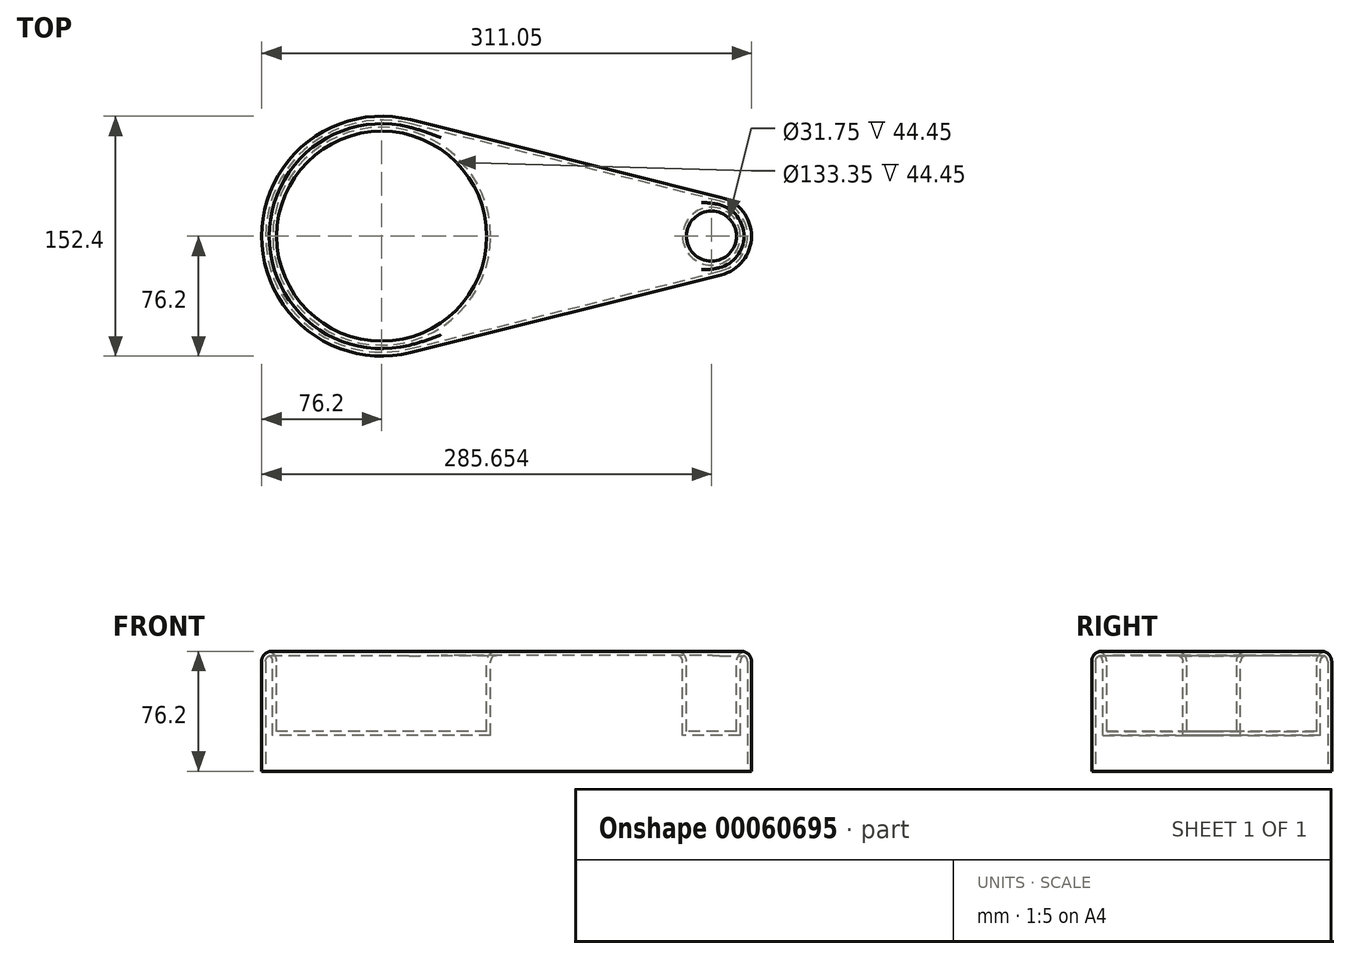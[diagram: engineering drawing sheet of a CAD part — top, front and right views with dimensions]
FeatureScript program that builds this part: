
annotation { "Feature Type Name" : "Feature", "Feature Type Description" : "" }
export const myFeature = defineFeature(function(context is Context, id is Id, definition is map)
    precondition{}
    {
        {
            var Q0;
            Q0=qCreatedBy(makeId("Top.planeOp"),FACE);
            var sketch = newSketch(context, id + "F0", { "sketchPlane" : qUnion([Q0])});
            skCircle(sketch, "E0", {"center": v(0, 0) * mm, "radius": 76.2 * mm});
            skCircle(sketch, "E1", {"center": v(209.45, 0) * mm, "radius": 25.4 * mm});
            skLineSegment(sketch, "E2", {"start": v(215.61, 24.64) * mm, "end": v(18.48, 73.92) * mm});
            skLineSegment(sketch, "E3", {"start": v(18.48, -73.92) * mm, "end": v(215.61, -24.64) * mm});
            skSolve(sketch);
        }
        {
            var Q0;
            {var subQ0=sQuery(id+"F0.wireOp",EDGE,"E0");var subQ1=makeQuery(id+"F0.imprint","INTERSECT",VERTEX,{"derivedFrom":[subQ0,sQuery(id+"F0.wireOp",EDGE,"E2")]});Q0=makeQuery(id+"F0.imprint","IMPRINT",FACE,{"disambiguationData":[TD([[makeQuery(id+"F0.imprint","IMPRINT",EDGE,{"disambiguationData":[TD([[subQ1,-1.0]])],"derivedFrom":subQ0}),1.0]])]});}
            var Q1;
            {var subQ0=sQuery(id+"F0.wireOp",EDGE,"E2");Q1=makeQuery(id+"F0.imprint","IMPRINT",FACE,{"disambiguationData":[TD([[makeQuery(id+"F0.imprint","IMPRINT",EDGE,{"derivedFrom":subQ0}),1.0]])]});}
            var Q2;
            {var subQ0=sQuery(id+"F0.wireOp",EDGE,"E1");var subQ1=makeQuery(id+"F0.imprint","INTERSECT",VERTEX,{"derivedFrom":[subQ0,sQuery(id+"F0.wireOp",EDGE,"E2")]});Q2=makeQuery(id+"F0.imprint","IMPRINT",FACE,{"disambiguationData":[TD([[makeQuery(id+"F0.imprint","IMPRINT",EDGE,{"disambiguationData":[TD([[subQ1,-1.0]])],"derivedFrom":subQ0}),1.0]])]});}
            extrude(context, id + "F1", {"entities" : qUnion([Q0, Q1, Q2]), "depth" : 3 * mm * 25.4});
        }
        {
            var Q0;
            Q0=makeQuery(id+"F1.opExtrude","CAP_FACE",FACE,{"disambiguationData":[OSD([sQuery(id+"F0.wireOp",EDGE,"E0"),sQuery(id+"F0.wireOp",EDGE,"E1"),sQuery(id+"F0.wireOp",EDGE,"E2"),sQuery(id+"F0.wireOp",EDGE,"E3")])],"isStart":false});
            var sketch = newSketch(context, id + "F2", { "sketchPlane" : qUnion([Q0])});
            skCircle(sketch, "E4", {"center": v(0, 0) * mm, "radius": 66.68 * mm});
            skCircle(sketch, "E5", {"center": v(209.45, 0) * mm, "radius": 15.88 * mm});
            skSolve(sketch);
        }
        {
            var Q0;
            Q0 = qSketchRegion(id + "F2", true);
            extrude(context, id + "F3", {"entities" : qUnion([Q0]), "operationType" : NewBodyOperationType.REMOVE, "oppositeDirection" : true, "depth" : 50.8 * mm});
        }
        {
            var Q0;
            Q0=makeQuery(id+"F1.opExtrude","CAP_FACE",FACE,{"disambiguationData":[OSD([sQuery(id+"F0.wireOp",EDGE,"E0"),sQuery(id+"F0.wireOp",EDGE,"E1"),sQuery(id+"F0.wireOp",EDGE,"E2"),sQuery(id+"F0.wireOp",EDGE,"E3")])],"isStart":false});
            fillet(context, id + "F4", {"entities" : qUnion([Q0]), "radius" : 6.35 * mm, "tangentPropagation" : true, "allowEdgeOverflow" : false});
        }
        {
            var Q0;
            Q0=makeQuery(id+"F1.opExtrude","CAP_FACE",FACE,{"disambiguationData":[OSD([sQuery(id+"F0.wireOp",EDGE,"E0"),sQuery(id+"F0.wireOp",EDGE,"E1"),sQuery(id+"F0.wireOp",EDGE,"E2"),sQuery(id+"F0.wireOp",EDGE,"E3")])],"isStart":true});
            shell(context, id + "F5", {"entities" : qUnion([Q0]), "thickness" : 2.5 * mm});
        }
    });
